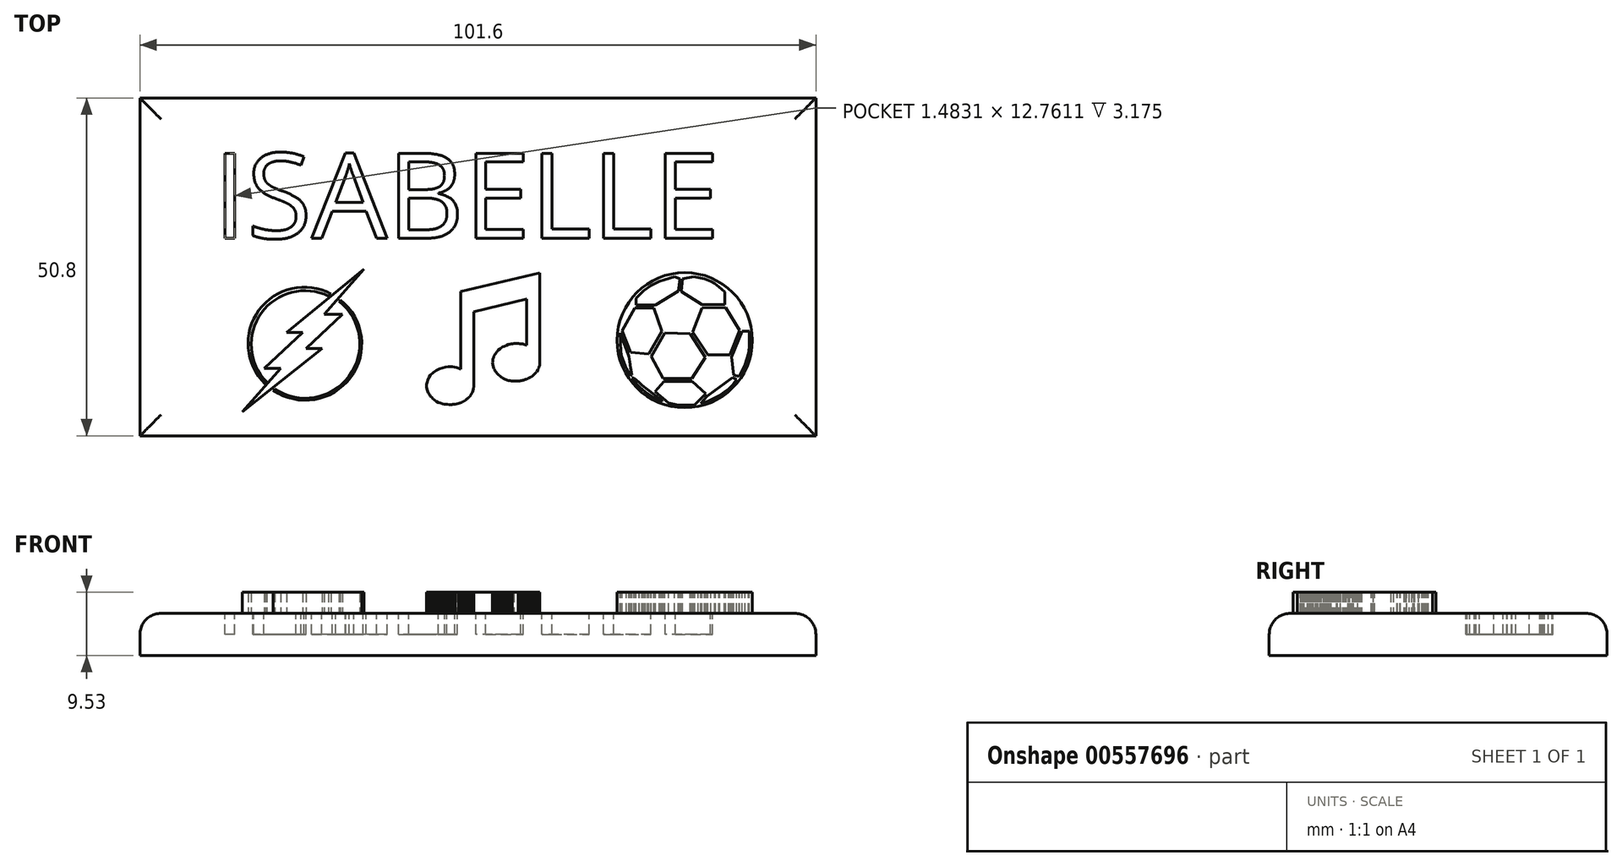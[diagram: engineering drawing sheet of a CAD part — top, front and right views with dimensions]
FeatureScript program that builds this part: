
annotation { "Feature Type Name" : "Feature", "Feature Type Description" : "" }
export const myFeature = defineFeature(function(context is Context, id is Id, definition is map)
    precondition{}
    {
        {
            var Q0;
            Q0=qCreatedBy(makeId("Top.planeOp"),FACE);
            var sketch = newSketch(context, id + "F0", { "sketchPlane" : qUnion([Q0])});
            skLineSegment(sketch, "E0.bottom", {"start": v(-50.9, 29.8) * mm, "end": v(50.7, 29.8) * mm});
            skLineSegment(sketch, "E0.top", {"start": v(-50.9, -21) * mm, "end": v(50.7, -21) * mm});
            skLineSegment(sketch, "E0.left", {"start": v(-50.9, 29.8) * mm, "end": v(-50.9, -21) * mm});
            skLineSegment(sketch, "E0.right", {"start": v(50.7, 29.8) * mm, "end": v(50.7, -21) * mm});
            skSolve(sketch);
        }
        {
            var Q0;
            Q0=makeQuery(id+"F0.imprint","IMPRINT",FACE,{"disambiguationData":[TD([[makeQuery(id+"F0.imprint","IMPRINT",EDGE,{"derivedFrom":sQuery(id+"F0.wireOp",EDGE,"E0.bottom")}),-1.0]])]});
            extrude(context, id + "F1", {"entities" : qUnion([Q0]), "depth" : 6.35 * mm, "offsetDistance" : 25.4 * mm});
        }
        {
            var Q0;
            Q0=makeQuery(id+"F1.opExtrude","CAP_FACE",FACE,{"disambiguationData":[OSD([sQuery(id+"F0.wireOp",EDGE,"E0.bottom"),sQuery(id+"F0.wireOp",EDGE,"E0.top"),sQuery(id+"F0.wireOp",EDGE,"E0.left"),sQuery(id+"F0.wireOp",EDGE,"E0.right")])],"isStart":false});
            var sketch = newSketch(context, id + "F2", { "sketchPlane" : qUnion([Q0])});
            skText(sketch, "E1", { "text": "ISABELLE", "fontName": "OpenSans-Regular.ttf"});
            const initialGuessF2  = {"E1": [-0.03987, 0.00873, 1, 0, 0.01287]};
            skSetInitialGuess(sketch, initialGuessF2);
            skSolve(sketch);
        }
        {
            var Q0;
            Q0 = qSketchRegion(id + "F2", true);
            extrude(context, id + "F3", {"entities" : qUnion([Q0]), "operationType" : NewBodyOperationType.REMOVE, "oppositeDirection" : true, "depth" : 3.17 * mm, "offsetDistance" : 25.4 * mm});
        }
        {
            var Q0;
            {var subQ0=sQuery(id+"F0.wireOp",EDGE,"E0.left");var subQ1=sQuery(id+"F0.wireOp",EDGE,"E0.bottom");var subQ2=sQuery(id+"F0.wireOp",EDGE,"E0.right");var subQ3=sQuery(id+"F0.wireOp",EDGE,"E0.top");Q0=makeQuery(id+"F3.boolean.opBoolean","SPLIT",FACE,{"disambiguationData":[TD([makeQuery(id+"F1.opExtrude","SWEPT_FACE",FACE,{"disambiguationData":[OSD([subQ1])]})])],"derivedFrom":makeQuery(id+"F1.opExtrude","CAP_FACE",FACE,{"disambiguationData":[OSD([subQ1,subQ3,subQ0,subQ2])],"isStart":false})});}
            var sketch = newSketch(context, id + "F4", { "sketchPlane" : qUnion([Q0])});
            skLineSegment(sketch, "E2", {"start": v(-35.49, -17.39) * mm, "end": v(-29.74, -10.84) * mm});
            skLineSegment(sketch, "E3", {"start": v(-29.74, -10.84) * mm, "end": v(-32.22, -10.84) * mm});
            skLineSegment(sketch, "E4", {"start": v(-32.22, -10.84) * mm, "end": v(-26.46, -5.43) * mm});
            skLineSegment(sketch, "E5", {"start": v(-26.46, -5.43) * mm, "end": v(-28.83, -5.43) * mm});
            skLineSegment(sketch, "E6", {"start": v(-28.83, -5.43) * mm, "end": v(-17.22, 4.04) * mm});
            skLineSegment(sketch, "E7", {"start": v(-17.22, 4.04) * mm, "end": v(-23.2, -2.75) * mm});
            skLineSegment(sketch, "E8", {"start": v(-23.2, -2.75) * mm, "end": v(-20.49, -2.75) * mm});
            skLineSegment(sketch, "E9", {"start": v(-20.49, -2.75) * mm, "end": v(-25.93, -7.87) * mm});
            skLineSegment(sketch, "E10", {"start": v(-25.93, -7.87) * mm, "end": v(-23.53, -7.87) * mm});
            skLineSegment(sketch, "E11", {"start": v(-23.53, -7.87) * mm, "end": v(-35.49, -17.39) * mm});
            skArc(sketch, "E12", {"start": v(-22.55, 0) * mm, "mid": v(-32.65, -2.52) * mm, "end": v(-31.86, -12.9) * mm});
            skLineSegment(sketch, "E13", {"start": v(-31.86, -12.9) * mm, "end": v(-32.08, -13.18) * mm});
            skArc(sketch, "E14", {"start": v(-22.17, 0.36) * mm, "mid": v(-33.02, -2.1) * mm, "end": v(-32.08, -13.18) * mm});
            skLineSegment(sketch, "E15", {"start": v(-22.55, 0) * mm, "end": v(-22.17, 0.36) * mm});
            skLineSegment(sketch, "E16", {"start": v(-20.95, -0.76) * mm, "end": v(-20.76, -0.55) * mm});
            skArc(sketch, "E17", {"start": v(-30.61, -13.93) * mm, "mid": v(-19.45, -12) * mm, "end": v(-20.95, -0.76) * mm});
            skLineSegment(sketch, "E18", {"start": v(-30.61, -13.93) * mm, "end": v(-30.87, -14.14) * mm});
            skArc(sketch, "E19", {"start": v(-30.87, -14.14) * mm, "mid": v(-19.25, -12.23) * mm, "end": v(-20.76, -0.55) * mm});
            skSolve(sketch);
        }
        {
            var Q0;
            Q0 = qSketchRegion(id + "F4", true);
            extrude(context, id + "F5", {"entities" : qUnion([Q0]), "operationType" : NewBodyOperationType.ADD, "depth" : 3.17 * mm, "offsetDistance" : 25.4 * mm});
        }
        {
            var Q0;
            {var subQ0=sQuery(id+"F0.wireOp",EDGE,"E0.left");var subQ1=sQuery(id+"F0.wireOp",EDGE,"E0.bottom");var subQ2=sQuery(id+"F0.wireOp",EDGE,"E0.right");var subQ3=sQuery(id+"F0.wireOp",EDGE,"E0.top");Q0=makeQuery(id+"F3.boolean.opBoolean","SPLIT",FACE,{"disambiguationData":[TD([makeQuery(id+"F1.opExtrude","SWEPT_FACE",FACE,{"disambiguationData":[OSD([subQ1])]})])],"derivedFrom":makeQuery(id+"F1.opExtrude","CAP_FACE",FACE,{"disambiguationData":[OSD([subQ1,subQ3,subQ0,subQ2])],"isStart":false})});}
            var sketch = newSketch(context, id + "F6", { "sketchPlane" : qUnion([Q0])});
            skCircle(sketch, "E20", {"center": v(30.98, -6.61) * mm, "radius": 10.16 * mm});
            skSolve(sketch);
        }
        {
            var Q0;
            Q0 = qSketchRegion(id + "F6", true);
            extrude(context, id + "F7", {"entities" : qUnion([Q0]), "operationType" : NewBodyOperationType.ADD, "depth" : 3.17 * mm, "offsetDistance" : 25.4 * mm});
        }
        {
            var Q0;
            Q0=makeQuery(id+"F7.opExtrude","CAP_FACE",FACE,{"disambiguationData":[OSD([sQuery(id+"F6.wireOp",EDGE,"E20")])],"isStart":false});
            var sketch = newSketch(context, id + "F8", { "sketchPlane" : qUnion([Q0])});
            skLineSegment(sketch, "E21", {"start": v(30.27, 2.59) * mm, "end": v(29.98, 0.79) * mm});
            skLineSegment(sketch, "E22", {"start": v(29.98, 0.79) * mm, "end": v(26.57, -1.35) * mm});
            skLineSegment(sketch, "E23", {"start": v(26.57, -1.35) * mm, "end": v(23.69, -1.35) * mm});
            skLineSegment(sketch, "E24", {"start": v(23.69, -1.35) * mm, "end": v(23.69, -0.3) * mm});
            skLineSegment(sketch, "E25", {"start": v(23.69, -0.3) * mm, "end": v(24.8, 0.84) * mm});
            skLineSegment(sketch, "E26", {"start": v(24.8, 0.84) * mm, "end": v(25.86, 1.57) * mm});
            skLineSegment(sketch, "E27", {"start": v(25.86, 1.57) * mm, "end": v(27.16, 2.22) * mm});
            skLineSegment(sketch, "E28", {"start": v(27.16, 2.22) * mm, "end": v(28, 2.5) * mm});
            skLineSegment(sketch, "E29", {"start": v(28, 2.5) * mm, "end": v(29.44, 2.92) * mm});
            skLineSegment(sketch, "E30", {"start": v(29.44, 2.92) * mm, "end": v(30.27, 2.59) * mm});
            skLineSegment(sketch, "E31", {"start": v(30.45, 0.68) * mm, "end": v(30.65, 2.59) * mm});
            skLineSegment(sketch, "E32", {"start": v(30.65, 2.59) * mm, "end": v(32.3, 2.92) * mm});
            skLineSegment(sketch, "E33", {"start": v(32.3, 2.92) * mm, "end": v(32.97, 2.8) * mm});
            skLineSegment(sketch, "E34", {"start": v(32.97, 2.8) * mm, "end": v(33.94, 2.59) * mm});
            skLineSegment(sketch, "E35", {"start": v(33.94, 2.59) * mm, "end": v(34.92, 2.2) * mm});
            skLineSegment(sketch, "E36", {"start": v(34.92, 2.2) * mm, "end": v(35.47, 1.94) * mm});
            skLineSegment(sketch, "E37", {"start": v(35.47, 1.94) * mm, "end": v(36.08, 1.4) * mm});
            skLineSegment(sketch, "E38", {"start": v(36.08, 1.4) * mm, "end": v(37.01, 0.63) * mm});
            skLineSegment(sketch, "E39", {"start": v(37.01, 0.63) * mm, "end": v(36.97, -1.28) * mm});
            skLineSegment(sketch, "E40", {"start": v(33.54, -1.28) * mm, "end": v(30.45, 0.68) * mm});
            skLineSegment(sketch, "E41", {"start": v(33.54, -1.28) * mm, "end": v(36.97, -1.28) * mm});
            skLineSegment(sketch, "E42", {"start": v(33.54, -1.76) * mm, "end": v(37.1, -1.73) * mm});
            skLineSegment(sketch, "E43", {"start": v(37.1, -1.73) * mm, "end": v(39.2, -5.15) * mm});
            skLineSegment(sketch, "E44", {"start": v(39.2, -5.15) * mm, "end": v(37.77, -8.8) * mm});
            skLineSegment(sketch, "E45", {"start": v(37.77, -8.8) * mm, "end": v(34.43, -8.8) * mm});
            skLineSegment(sketch, "E46", {"start": v(34.43, -8.8) * mm, "end": v(32.15, -5.37) * mm});
            skLineSegment(sketch, "E47", {"start": v(32.15, -5.37) * mm, "end": v(33.54, -1.76) * mm});
            skLineSegment(sketch, "E48", {"start": v(31.82, -5.63) * mm, "end": v(27.97, -5.53) * mm});
            skLineSegment(sketch, "E49", {"start": v(27.97, -5.53) * mm, "end": v(25.93, -9.06) * mm});
            skLineSegment(sketch, "E50", {"start": v(25.93, -9.06) * mm, "end": v(27.73, -12.36) * mm});
            skLineSegment(sketch, "E51", {"start": v(27.73, -12.36) * mm, "end": v(32.02, -12.36) * mm});
            skLineSegment(sketch, "E52", {"start": v(32.02, -12.36) * mm, "end": v(34.05, -9.17) * mm});
            skLineSegment(sketch, "E53", {"start": v(34.05, -9.17) * mm, "end": v(31.82, -5.63) * mm});
            skLineSegment(sketch, "E54", {"start": v(26.33, -1.76) * mm, "end": v(23.45, -1.76) * mm});
            skLineSegment(sketch, "E55", {"start": v(23.45, -1.76) * mm, "end": v(21.59, -5.2) * mm});
            skLineSegment(sketch, "E56", {"start": v(21.59, -5.2) * mm, "end": v(22.83, -8.47) * mm});
            skLineSegment(sketch, "E57", {"start": v(22.83, -8.47) * mm, "end": v(25.6, -8.67) * mm});
            skLineSegment(sketch, "E58", {"start": v(25.6, -8.67) * mm, "end": v(27.57, -5.25) * mm});
            skLineSegment(sketch, "E59", {"start": v(27.57, -5.25) * mm, "end": v(26.33, -1.76) * mm});
            skLineSegment(sketch, "E60", {"start": v(21.26, -5.53) * mm, "end": v(21.35, -8.3) * mm});
            skLineSegment(sketch, "E61", {"start": v(21.35, -8.3) * mm, "end": v(21.5, -9.06) * mm});
            skLineSegment(sketch, "E62", {"start": v(21.5, -9.06) * mm, "end": v(21.93, -10.2) * mm});
            skLineSegment(sketch, "E63", {"start": v(21.93, -10.2) * mm, "end": v(22.2, -10.89) * mm});
            skLineSegment(sketch, "E64", {"start": v(22.2, -10.89) * mm, "end": v(22.62, -11.7) * mm});
            skLineSegment(sketch, "E65", {"start": v(22.62, -11.7) * mm, "end": v(22.8, -11.98) * mm});
            skLineSegment(sketch, "E66", {"start": v(22.8, -11.98) * mm, "end": v(23.06, -11.89) * mm});
            skLineSegment(sketch, "E67", {"start": v(23.06, -11.89) * mm, "end": v(22.85, -10.76) * mm});
            skLineSegment(sketch, "E68", {"start": v(22.85, -10.76) * mm, "end": v(22.7, -9.8) * mm});
            skLineSegment(sketch, "E69", {"start": v(22.7, -9.8) * mm, "end": v(22.6, -9.06) * mm});
            skLineSegment(sketch, "E70", {"start": v(22.6, -9.06) * mm, "end": v(22.2, -8.01) * mm});
            skLineSegment(sketch, "E71", {"start": v(22.2, -8.01) * mm, "end": v(21.26, -5.53) * mm});
            skLineSegment(sketch, "E72", {"start": v(23.06, -12.31) * mm, "end": v(23.33, -12.31) * mm});
            skLineSegment(sketch, "E73", {"start": v(23.33, -12.31) * mm, "end": v(24.08, -12.94) * mm});
            skLineSegment(sketch, "E74", {"start": v(24.08, -12.94) * mm, "end": v(24.55, -13.36) * mm});
            skLineSegment(sketch, "E75", {"start": v(24.55, -13.36) * mm, "end": v(25.38, -14.05) * mm});
            skLineSegment(sketch, "E76", {"start": v(25.38, -14.05) * mm, "end": v(26.44, -14.86) * mm});
            skLineSegment(sketch, "E77", {"start": v(26.44, -14.86) * mm, "end": v(27.62, -15.77) * mm});
            skLineSegment(sketch, "E78", {"start": v(27.62, -15.77) * mm, "end": v(27.6, -15.82) * mm});
            skLineSegment(sketch, "E79", {"start": v(27.6, -15.82) * mm, "end": v(27.29, -15.72) * mm});
            skLineSegment(sketch, "E80", {"start": v(27.29, -15.72) * mm, "end": v(26.4, -15.27) * mm});
            skLineSegment(sketch, "E81", {"start": v(26.4, -15.27) * mm, "end": v(25.07, -14.43) * mm});
            skLineSegment(sketch, "E82", {"start": v(25.07, -14.43) * mm, "end": v(24.2, -13.64) * mm});
            skLineSegment(sketch, "E83", {"start": v(24.2, -13.64) * mm, "end": v(23.34, -12.74) * mm});
            skLineSegment(sketch, "E84", {"start": v(23.34, -12.74) * mm, "end": v(23.06, -12.31) * mm});
            skLineSegment(sketch, "E85", {"start": v(26.53, -14.37) * mm, "end": v(27.88, -12.85) * mm});
            skLineSegment(sketch, "E86", {"start": v(27.88, -12.85) * mm, "end": v(32.09, -12.85) * mm});
            skLineSegment(sketch, "E87", {"start": v(32.09, -12.85) * mm, "end": v(34.13, -14.66) * mm});
            skLineSegment(sketch, "E88", {"start": v(34.13, -14.66) * mm, "end": v(32.51, -16.3) * mm});
            skLineSegment(sketch, "E89", {"start": v(32.51, -16.3) * mm, "end": v(30.03, -16.35) * mm});
            skLineSegment(sketch, "E90", {"start": v(30.03, -16.35) * mm, "end": v(28.58, -16.08) * mm});
            skLineSegment(sketch, "E91", {"start": v(28.58, -16.08) * mm, "end": v(26.53, -14.37) * mm});
            skLineSegment(sketch, "E92", {"start": v(39.63, -5.29) * mm, "end": v(40.67, -5.29) * mm});
            skLineSegment(sketch, "E93", {"start": v(40.67, -5.29) * mm, "end": v(40.67, -7.67) * mm});
            skLineSegment(sketch, "E94", {"start": v(40.67, -7.67) * mm, "end": v(40.52, -8.6) * mm});
            skLineSegment(sketch, "E95", {"start": v(40.52, -8.6) * mm, "end": v(40.05, -10.3) * mm});
            skLineSegment(sketch, "E96", {"start": v(40.05, -10.3) * mm, "end": v(39.17, -12.03) * mm});
            skLineSegment(sketch, "E97", {"start": v(39.17, -12.03) * mm, "end": v(38.31, -11.84) * mm});
            skLineSegment(sketch, "E98", {"start": v(38.31, -11.84) * mm, "end": v(38, -9.14) * mm});
            skLineSegment(sketch, "E99", {"start": v(38, -9.14) * mm, "end": v(39.63, -5.29) * mm});
            skLineSegment(sketch, "E100", {"start": v(38.11, -12.26) * mm, "end": v(38.8, -12.5) * mm});
            skLineSegment(sketch, "E101", {"start": v(38.8, -12.5) * mm, "end": v(38.19, -13.33) * mm});
            skLineSegment(sketch, "E102", {"start": v(38.19, -13.33) * mm, "end": v(37.55, -13.93) * mm});
            skLineSegment(sketch, "E103", {"start": v(37.55, -13.93) * mm, "end": v(36.93, -14.42) * mm});
            skLineSegment(sketch, "E104", {"start": v(36.93, -14.42) * mm, "end": v(36.23, -14.9) * mm});
            skLineSegment(sketch, "E105", {"start": v(36.23, -14.9) * mm, "end": v(35.6, -15.26) * mm});
            skLineSegment(sketch, "E106", {"start": v(35.6, -15.26) * mm, "end": v(34.44, -15.78) * mm});
            skLineSegment(sketch, "E107", {"start": v(34.44, -15.78) * mm, "end": v(33.35, -16.1) * mm});
            skLineSegment(sketch, "E108", {"start": v(33.35, -16.1) * mm, "end": v(34.35, -15.02) * mm});
            skLineSegment(sketch, "E109", {"start": v(34.35, -15.02) * mm, "end": v(35.55, -14.16) * mm});
            skLineSegment(sketch, "E110", {"start": v(35.55, -14.16) * mm, "end": v(36.93, -13.16) * mm});
            skLineSegment(sketch, "E111", {"start": v(36.93, -13.16) * mm, "end": v(38.11, -12.26) * mm});
            skPoint(sketch, "E112.endSnap0", {"position": v(34.95, -14.59) * mm});
            skSolve(sketch);
        }
        {
            var Q0;
            Q0 = qSketchRegion(id + "F8", true);
            extrude(context, id + "F9", {"entities" : qUnion([Q0]), "operationType" : NewBodyOperationType.REMOVE, "oppositeDirection" : true, "depth" : 3.17 * mm, "offsetDistance" : 25.4 * mm});
        }
        {
            var Q0;
            {var subQ0=sQuery(id+"F0.wireOp",EDGE,"E0.left");var subQ1=sQuery(id+"F0.wireOp",EDGE,"E0.bottom");var subQ2=sQuery(id+"F0.wireOp",EDGE,"E0.right");var subQ3=sQuery(id+"F0.wireOp",EDGE,"E0.top");Q0=makeQuery(id+"F3.boolean.opBoolean","SPLIT",FACE,{"disambiguationData":[TD([makeQuery(id+"F1.opExtrude","SWEPT_FACE",FACE,{"disambiguationData":[OSD([subQ1])]})])],"derivedFrom":makeQuery(id+"F1.opExtrude","CAP_FACE",FACE,{"disambiguationData":[OSD([subQ1,subQ3,subQ0,subQ2])],"isStart":false})});}
            var sketch = newSketch(context, id + "F10", { "sketchPlane" : qUnion([Q0])});
            skLineSegment(sketch, "E113", {"start": v(-2.7, -10.98) * mm, "end": v(-2.96, -10.85) * mm});
            skLineSegment(sketch, "E114", {"start": v(-2.96, -10.85) * mm, "end": v(-3.32, -10.74) * mm});
            skLineSegment(sketch, "E115", {"start": v(-3.32, -10.74) * mm, "end": v(-3.65, -10.68) * mm});
            skLineSegment(sketch, "E116", {"start": v(-3.65, -10.68) * mm, "end": v(-3.97, -10.62) * mm});
            skLineSegment(sketch, "E117", {"start": v(-3.97, -10.62) * mm, "end": v(-4.3, -10.62) * mm});
            skLineSegment(sketch, "E118", {"start": v(-4.3, -10.62) * mm, "end": v(-4.6, -10.62) * mm});
            skLineSegment(sketch, "E119", {"start": v(-4.6, -10.62) * mm, "end": v(-4.97, -10.68) * mm});
            skLineSegment(sketch, "E120", {"start": v(-4.97, -10.68) * mm, "end": v(-5.42, -10.77) * mm});
            skLineSegment(sketch, "E121", {"start": v(-5.42, -10.77) * mm, "end": v(-5.89, -10.93) * mm});
            skLineSegment(sketch, "E122", {"start": v(-5.89, -10.93) * mm, "end": v(-6.37, -11.19) * mm});
            skLineSegment(sketch, "E123", {"start": v(-6.37, -11.19) * mm, "end": v(-6.85, -11.5) * mm});
            skLineSegment(sketch, "E124", {"start": v(-6.85, -11.5) * mm, "end": v(-7.23, -11.9) * mm});
            skLineSegment(sketch, "E125", {"start": v(-7.23, -11.9) * mm, "end": v(-7.44, -12.18) * mm});
            skLineSegment(sketch, "E126", {"start": v(-7.44, -12.18) * mm, "end": v(-7.65, -12.63) * mm});
            skLineSegment(sketch, "E127", {"start": v(-7.65, -12.63) * mm, "end": v(-7.74, -12.9) * mm});
            skLineSegment(sketch, "E128", {"start": v(-7.74, -12.9) * mm, "end": v(-7.83, -13.29) * mm});
            skLineSegment(sketch, "E129", {"start": v(-7.83, -13.29) * mm, "end": v(-7.83, -13.73) * mm});
            skLineSegment(sketch, "E130", {"start": v(-7.83, -13.73) * mm, "end": v(-7.74, -14.13) * mm});
            skLineSegment(sketch, "E131", {"start": v(-7.74, -14.13) * mm, "end": v(-7.57, -14.53) * mm});
            skLineSegment(sketch, "E132", {"start": v(-7.57, -14.53) * mm, "end": v(-7.43, -14.76) * mm});
            skLineSegment(sketch, "E133", {"start": v(-7.43, -14.76) * mm, "end": v(-7.36, -14.88) * mm});
            skLineSegment(sketch, "E134", {"start": v(-7.36, -14.88) * mm, "end": v(-7.24, -15.03) * mm});
            skLineSegment(sketch, "E135", {"start": v(-7.24, -15.03) * mm, "end": v(-7.1, -15.19) * mm});
            skLineSegment(sketch, "E136", {"start": v(-7.1, -15.19) * mm, "end": v(-7.04, -15.26) * mm});
            skLineSegment(sketch, "E137", {"start": v(-7.04, -15.26) * mm, "end": v(-6.89, -15.4) * mm});
            skLineSegment(sketch, "E138", {"start": v(-6.89, -15.4) * mm, "end": v(-6.72, -15.53) * mm});
            skLineSegment(sketch, "E139", {"start": v(-6.72, -15.53) * mm, "end": v(-6.53, -15.67) * mm});
            skLineSegment(sketch, "E140", {"start": v(-6.53, -15.67) * mm, "end": v(-6.36, -15.8) * mm});
            skLineSegment(sketch, "E141", {"start": v(-6.36, -15.8) * mm, "end": v(-6.04, -15.96) * mm});
            skLineSegment(sketch, "E142", {"start": v(-6.04, -15.96) * mm, "end": v(-5.74, -16.09) * mm});
            skLineSegment(sketch, "E143", {"start": v(-5.74, -16.09) * mm, "end": v(-5.42, -16.2) * mm});
            skLineSegment(sketch, "E144", {"start": v(-5.42, -16.2) * mm, "end": v(-5.14, -16.25) * mm});
            skLineSegment(sketch, "E145", {"start": v(-5.14, -16.25) * mm, "end": v(-4.88, -16.28) * mm});
            skLineSegment(sketch, "E146", {"start": v(-4.88, -16.28) * mm, "end": v(-4.69, -16.28) * mm});
            skLineSegment(sketch, "E147", {"start": v(-4.69, -16.28) * mm, "end": v(-4.55, -16.3) * mm});
            skLineSegment(sketch, "E148", {"start": v(-4.55, -16.3) * mm, "end": v(-4.39, -16.3) * mm});
            skLineSegment(sketch, "E149", {"start": v(-4.39, -16.3) * mm, "end": v(-4.22, -16.3) * mm});
            skLineSegment(sketch, "E150", {"start": v(-4.22, -16.3) * mm, "end": v(-4, -16.3) * mm});
            skLineSegment(sketch, "E151", {"start": v(-4, -16.3) * mm, "end": v(-3.87, -16.28) * mm});
            skLineSegment(sketch, "E152", {"start": v(-3.87, -16.28) * mm, "end": v(-3.68, -16.26) * mm});
            skLineSegment(sketch, "E153", {"start": v(-3.68, -16.26) * mm, "end": v(-3.5, -16.22) * mm});
            skLineSegment(sketch, "E154", {"start": v(-3.5, -16.22) * mm, "end": v(-3.35, -16.19) * mm});
            skLineSegment(sketch, "E155", {"start": v(-3.35, -16.19) * mm, "end": v(-3.19, -16.15) * mm});
            skLineSegment(sketch, "E156", {"start": v(-3.19, -16.15) * mm, "end": v(-3.02, -16.11) * mm});
            skLineSegment(sketch, "E157", {"start": v(-3.02, -16.11) * mm, "end": v(-2.87, -16.07) * mm});
            skLineSegment(sketch, "E158", {"start": v(-2.87, -16.07) * mm, "end": v(-2.76, -16.03) * mm});
            skLineSegment(sketch, "E159", {"start": v(-2.76, -16.03) * mm, "end": v(-2.65, -16) * mm});
            skLineSegment(sketch, "E160", {"start": v(-2.65, -16) * mm, "end": v(-2.56, -15.95) * mm});
            skLineSegment(sketch, "E161", {"start": v(-2.56, -15.95) * mm, "end": v(-2.46, -15.9) * mm});
            skLineSegment(sketch, "E162", {"start": v(-2.46, -15.9) * mm, "end": v(-2.37, -15.86) * mm});
            skLineSegment(sketch, "E163", {"start": v(-2.37, -15.86) * mm, "end": v(-2.27, -15.81) * mm});
            skLineSegment(sketch, "E164", {"start": v(-2.27, -15.81) * mm, "end": v(-2.2, -15.77) * mm});
            skLineSegment(sketch, "E165", {"start": v(-2.2, -15.77) * mm, "end": v(-2.14, -15.74) * mm});
            skLineSegment(sketch, "E166", {"start": v(-2.14, -15.74) * mm, "end": v(-2.08, -15.7) * mm});
            skLineSegment(sketch, "E167", {"start": v(-2.08, -15.7) * mm, "end": v(-2.01, -15.65) * mm});
            skLineSegment(sketch, "E168", {"start": v(-2.01, -15.65) * mm, "end": v(-1.96, -15.62) * mm});
            skLineSegment(sketch, "E169", {"start": v(-1.96, -15.62) * mm, "end": v(-1.92, -15.59) * mm});
            skLineSegment(sketch, "E170", {"start": v(-1.92, -15.59) * mm, "end": v(-1.9, -15.56) * mm});
            skLineSegment(sketch, "E171", {"start": v(-1.9, -15.56) * mm, "end": v(-1.84, -15.53) * mm});
            skLineSegment(sketch, "E172", {"start": v(-1.84, -15.53) * mm, "end": v(-1.79, -15.5) * mm});
            skLineSegment(sketch, "E173", {"start": v(-1.79, -15.5) * mm, "end": v(-1.75, -15.45) * mm});
            skLineSegment(sketch, "E174", {"start": v(-1.75, -15.45) * mm, "end": v(-1.7, -15.42) * mm});
            skLineSegment(sketch, "E175", {"start": v(-1.7, -15.42) * mm, "end": v(-1.67, -15.38) * mm});
            skLineSegment(sketch, "E176", {"start": v(-1.67, -15.38) * mm, "end": v(-1.63, -15.34) * mm});
            skLineSegment(sketch, "E177", {"start": v(-1.63, -15.34) * mm, "end": v(-1.59, -15.3) * mm});
            skLineSegment(sketch, "E178", {"start": v(-1.59, -15.3) * mm, "end": v(-1.55, -15.28) * mm});
            skLineSegment(sketch, "E179", {"start": v(-1.55, -15.28) * mm, "end": v(-1.52, -15.23) * mm});
            skLineSegment(sketch, "E180", {"start": v(-1.52, -15.23) * mm, "end": v(-1.48, -15.2) * mm});
            skLineSegment(sketch, "E181", {"start": v(-1.48, -15.2) * mm, "end": v(-1.43, -15.16) * mm});
            skLineSegment(sketch, "E182", {"start": v(-1.43, -15.16) * mm, "end": v(-1.41, -15.13) * mm});
            skLineSegment(sketch, "E183", {"start": v(-1.41, -15.13) * mm, "end": v(-1.38, -15.09) * mm});
            skLineSegment(sketch, "E184", {"start": v(-1.38, -15.09) * mm, "end": v(-1.34, -15.05) * mm});
            skLineSegment(sketch, "E185", {"start": v(-1.34, -15.05) * mm, "end": v(-1.3, -15.01) * mm});
            skLineSegment(sketch, "E186", {"start": v(-1.3, -15.01) * mm, "end": v(-1.26, -14.96) * mm});
            skLineSegment(sketch, "E187", {"start": v(-1.26, -14.96) * mm, "end": v(-1.22, -14.9) * mm});
            skLineSegment(sketch, "E188", {"start": v(-1.22, -14.9) * mm, "end": v(-1.17, -14.85) * mm});
            skLineSegment(sketch, "E189", {"start": v(-1.17, -14.85) * mm, "end": v(-1.14, -14.8) * mm});
            skLineSegment(sketch, "E190", {"start": v(-1.14, -14.8) * mm, "end": v(-1.1, -14.76) * mm});
            skLineSegment(sketch, "E191", {"start": v(-1.1, -14.76) * mm, "end": v(-1.07, -14.7) * mm});
            skLineSegment(sketch, "E192", {"start": v(-1.07, -14.7) * mm, "end": v(-1.05, -14.66) * mm});
            skLineSegment(sketch, "E193", {"start": v(-1.05, -14.66) * mm, "end": v(-1.02, -14.62) * mm});
            skLineSegment(sketch, "E194", {"start": v(-1.02, -14.62) * mm, "end": v(-1, -14.57) * mm});
            skLineSegment(sketch, "E195", {"start": v(-1, -14.57) * mm, "end": v(-0.96, -14.5) * mm});
            skLineSegment(sketch, "E196", {"start": v(-0.96, -14.5) * mm, "end": v(-0.95, -14.46) * mm});
            skLineSegment(sketch, "E197", {"start": v(-0.95, -14.46) * mm, "end": v(-0.92, -14.41) * mm});
            skLineSegment(sketch, "E198", {"start": v(-0.92, -14.41) * mm, "end": v(-0.9, -14.38) * mm});
            skLineSegment(sketch, "E199", {"start": v(-0.9, -14.38) * mm, "end": v(-0.9, -14.33) * mm});
            skLineSegment(sketch, "E200", {"start": v(-0.9, -14.33) * mm, "end": v(-0.86, -14.22) * mm});
            skLineSegment(sketch, "E201", {"start": v(-0.86, -14.22) * mm, "end": v(-0.8, -14.09) * mm});
            skLineSegment(sketch, "E202", {"start": v(-0.8, -14.09) * mm, "end": v(-0.76, -13.94) * mm});
            skLineSegment(sketch, "E203", {"start": v(-0.76, -13.94) * mm, "end": v(-0.75, -13.81) * mm});
            skLineSegment(sketch, "E204", {"start": v(-0.75, -13.81) * mm, "end": v(-0.73, -13.69) * mm});
            skLineSegment(sketch, "E205", {"start": v(-0.73, -13.69) * mm, "end": v(-0.72, -13.54) * mm});
            skLineSegment(sketch, "E206", {"start": v(-0.72, -13.54) * mm, "end": v(-0.72, -13.4) * mm});
            skLineSegment(sketch, "E207", {"start": v(-0.72, -13.4) * mm, "end": v(-0.72, -13.18) * mm});
            skLineSegment(sketch, "E208", {"start": v(-0.72, -13.18) * mm, "end": v(-0.72, -12.82) * mm});
            skLineSegment(sketch, "E209", {"start": v(-0.72, -12.82) * mm, "end": v(-0.72, -2.34) * mm});
            skLineSegment(sketch, "E210", {"start": v(-0.72, -2.34) * mm, "end": v(7.16, -0.44) * mm});
            skLineSegment(sketch, "E211", {"start": v(7.16, -0.44) * mm, "end": v(7.22, -0.44) * mm});
            skLineSegment(sketch, "E212", {"start": v(7.22, -0.44) * mm, "end": v(7.22, -7.38) * mm});
            skLineSegment(sketch, "E213", {"start": v(7.22, -7.38) * mm, "end": v(7.13, -7.35) * mm});
            skLineSegment(sketch, "E214", {"start": v(7.13, -7.35) * mm, "end": v(7.03, -7.32) * mm});
            skLineSegment(sketch, "E215", {"start": v(7.03, -7.32) * mm, "end": v(6.95, -7.29) * mm});
            skLineSegment(sketch, "E216", {"start": v(6.95, -7.29) * mm, "end": v(6.86, -7.26) * mm});
            skLineSegment(sketch, "E217", {"start": v(6.86, -7.26) * mm, "end": v(6.76, -7.22) * mm});
            skLineSegment(sketch, "E218", {"start": v(6.76, -7.22) * mm, "end": v(6.64, -7.2) * mm});
            skLineSegment(sketch, "E219", {"start": v(6.64, -7.2) * mm, "end": v(6.52, -7.17) * mm});
            skLineSegment(sketch, "E220", {"start": v(6.52, -7.17) * mm, "end": v(6.4, -7.16) * mm});
            skLineSegment(sketch, "E221", {"start": v(6.4, -7.16) * mm, "end": v(6.27, -7.15) * mm});
            skLineSegment(sketch, "E222", {"start": v(6.27, -7.15) * mm, "end": v(6.16, -7.14) * mm});
            skLineSegment(sketch, "E223", {"start": v(6.16, -7.14) * mm, "end": v(6.04, -7.11) * mm});
            skLineSegment(sketch, "E224", {"start": v(6.04, -7.11) * mm, "end": v(5.9, -7.11) * mm});
            skLineSegment(sketch, "E225", {"start": v(5.9, -7.11) * mm, "end": v(5.77, -7.11) * mm});
            skLineSegment(sketch, "E226", {"start": v(5.77, -7.11) * mm, "end": v(5.48, -7.11) * mm});
            skLineSegment(sketch, "E227", {"start": v(5.48, -7.11) * mm, "end": v(5.3, -7.11) * mm});
            skLineSegment(sketch, "E228", {"start": v(5.3, -7.11) * mm, "end": v(5.23, -7.13) * mm});
            skLineSegment(sketch, "E229", {"start": v(5.23, -7.13) * mm, "end": v(5.17, -7.15) * mm});
            skLineSegment(sketch, "E230", {"start": v(5.17, -7.15) * mm, "end": v(5.12, -7.15) * mm});
            skLineSegment(sketch, "E231", {"start": v(5.12, -7.15) * mm, "end": v(5.04, -7.16) * mm});
            skLineSegment(sketch, "E232", {"start": v(5.04, -7.16) * mm, "end": v(5, -7.16) * mm});
            skLineSegment(sketch, "E233", {"start": v(5, -7.16) * mm, "end": v(4.94, -7.18) * mm});
            skLineSegment(sketch, "E234", {"start": v(4.94, -7.18) * mm, "end": v(4.89, -7.19) * mm});
            skLineSegment(sketch, "E235", {"start": v(4.89, -7.19) * mm, "end": v(4.85, -7.2) * mm});
            skLineSegment(sketch, "E236", {"start": v(4.85, -7.2) * mm, "end": v(4.8, -7.2) * mm});
            skLineSegment(sketch, "E237", {"start": v(4.8, -7.2) * mm, "end": v(4.76, -7.2) * mm});
            skLineSegment(sketch, "E238", {"start": v(4.76, -7.2) * mm, "end": v(4.72, -7.21) * mm});
            skLineSegment(sketch, "E239", {"start": v(4.72, -7.21) * mm, "end": v(4.7, -7.22) * mm});
            skLineSegment(sketch, "E240", {"start": v(4.7, -7.22) * mm, "end": v(4.66, -7.23) * mm});
            skLineSegment(sketch, "E241", {"start": v(4.66, -7.23) * mm, "end": v(4.62, -7.23) * mm});
            skLineSegment(sketch, "E242", {"start": v(4.62, -7.23) * mm, "end": v(4.58, -7.24) * mm});
            skLineSegment(sketch, "E243", {"start": v(4.58, -7.24) * mm, "end": v(4.5, -7.25) * mm});
            skLineSegment(sketch, "E244", {"start": v(4.5, -7.25) * mm, "end": v(4.41, -7.29) * mm});
            skLineSegment(sketch, "E245", {"start": v(4.41, -7.29) * mm, "end": v(4.29, -7.34) * mm});
            skLineSegment(sketch, "E246", {"start": v(4.29, -7.34) * mm, "end": v(4.16, -7.4) * mm});
            skLineSegment(sketch, "E247", {"start": v(4.16, -7.4) * mm, "end": v(4.05, -7.42) * mm});
            skLineSegment(sketch, "E248", {"start": v(4.05, -7.42) * mm, "end": v(3.96, -7.46) * mm});
            skLineSegment(sketch, "E249", {"start": v(3.96, -7.46) * mm, "end": v(3.86, -7.53) * mm});
            skLineSegment(sketch, "E250", {"start": v(3.86, -7.53) * mm, "end": v(3.77, -7.57) * mm});
            skLineSegment(sketch, "E251", {"start": v(3.77, -7.57) * mm, "end": v(3.62, -7.64) * mm});
            skLineSegment(sketch, "E252", {"start": v(3.62, -7.64) * mm, "end": v(3.49, -7.73) * mm});
            skLineSegment(sketch, "E253", {"start": v(3.49, -7.73) * mm, "end": v(3.39, -7.8) * mm});
            skLineSegment(sketch, "E254", {"start": v(3.39, -7.8) * mm, "end": v(3.3, -7.87) * mm});
            skLineSegment(sketch, "E255", {"start": v(3.3, -7.87) * mm, "end": v(3.2, -7.91) * mm});
            skLineSegment(sketch, "E256", {"start": v(3.2, -7.91) * mm, "end": v(3.12, -7.97) * mm});
            skLineSegment(sketch, "E257", {"start": v(3.12, -7.97) * mm, "end": v(3, -8.05) * mm});
            skLineSegment(sketch, "E258", {"start": v(3, -8.05) * mm, "end": v(2.9, -8.13) * mm});
            skLineSegment(sketch, "E259", {"start": v(2.9, -8.13) * mm, "end": v(2.87, -8.2) * mm});
            skLineSegment(sketch, "E260", {"start": v(2.87, -8.2) * mm, "end": v(2.78, -8.3) * mm});
            skLineSegment(sketch, "E261", {"start": v(2.78, -8.3) * mm, "end": v(2.68, -8.42) * mm});
            skLineSegment(sketch, "E262", {"start": v(2.68, -8.42) * mm, "end": v(2.62, -8.51) * mm});
            skLineSegment(sketch, "E263", {"start": v(2.62, -8.51) * mm, "end": v(2.54, -8.64) * mm});
            skLineSegment(sketch, "E264", {"start": v(2.54, -8.64) * mm, "end": v(2.47, -8.74) * mm});
            skLineSegment(sketch, "E265", {"start": v(2.47, -8.74) * mm, "end": v(2.43, -8.8) * mm});
            skLineSegment(sketch, "E266", {"start": v(2.43, -8.8) * mm, "end": v(2.39, -8.87) * mm});
            skLineSegment(sketch, "E267", {"start": v(2.39, -8.87) * mm, "end": v(2.35, -8.93) * mm});
            skLineSegment(sketch, "E268", {"start": v(2.35, -8.93) * mm, "end": v(2.33, -9) * mm});
            skLineSegment(sketch, "E269", {"start": v(2.33, -9) * mm, "end": v(2.28, -9.09) * mm});
            skLineSegment(sketch, "E270", {"start": v(2.28, -9.09) * mm, "end": v(2.25, -9.18) * mm});
            skLineSegment(sketch, "E271", {"start": v(2.25, -9.18) * mm, "end": v(2.22, -9.27) * mm});
            skLineSegment(sketch, "E272", {"start": v(2.22, -9.27) * mm, "end": v(2.2, -9.33) * mm});
            skLineSegment(sketch, "E273", {"start": v(2.2, -9.33) * mm, "end": v(2.19, -9.4) * mm});
            skLineSegment(sketch, "E274", {"start": v(2.19, -9.4) * mm, "end": v(2.17, -9.46) * mm});
            skLineSegment(sketch, "E275", {"start": v(2.17, -9.46) * mm, "end": v(2.17, -9.56) * mm});
            skLineSegment(sketch, "E276", {"start": v(2.17, -9.56) * mm, "end": v(2.15, -9.63) * mm});
            skLineSegment(sketch, "E277", {"start": v(2.15, -9.63) * mm, "end": v(2.12, -9.72) * mm});
            skLineSegment(sketch, "E278", {"start": v(2.12, -9.72) * mm, "end": v(2.12, -9.82) * mm});
            skLineSegment(sketch, "E279", {"start": v(2.12, -9.82) * mm, "end": v(2.1, -9.9) * mm});
            skLineSegment(sketch, "E280", {"start": v(2.1, -9.9) * mm, "end": v(2.08, -9.99) * mm});
            skLineSegment(sketch, "E281", {"start": v(2.08, -9.99) * mm, "end": v(2.1, -10.08) * mm});
            skLineSegment(sketch, "E282", {"start": v(2.1, -10.08) * mm, "end": v(2.1, -10.19) * mm});
            skLineSegment(sketch, "E283", {"start": v(2.1, -10.19) * mm, "end": v(2.12, -10.27) * mm});
            skLineSegment(sketch, "E284", {"start": v(2.12, -10.27) * mm, "end": v(2.14, -10.39) * mm});
            skLineSegment(sketch, "E285", {"start": v(2.14, -10.39) * mm, "end": v(2.16, -10.5) * mm});
            skLineSegment(sketch, "E286", {"start": v(2.16, -10.5) * mm, "end": v(2.18, -10.6) * mm});
            skLineSegment(sketch, "E287", {"start": v(2.18, -10.6) * mm, "end": v(2.2, -10.66) * mm});
            skLineSegment(sketch, "E288", {"start": v(2.2, -10.66) * mm, "end": v(2.25, -10.77) * mm});
            skLineSegment(sketch, "E289", {"start": v(2.25, -10.77) * mm, "end": v(2.3, -10.9) * mm});
            skLineSegment(sketch, "E290", {"start": v(2.3, -10.9) * mm, "end": v(2.36, -11) * mm});
            skLineSegment(sketch, "E291", {"start": v(2.36, -11) * mm, "end": v(2.39, -11.05) * mm});
            skLineSegment(sketch, "E292", {"start": v(2.39, -11.05) * mm, "end": v(2.43, -11.15) * mm});
            skLineSegment(sketch, "E293", {"start": v(2.43, -11.15) * mm, "end": v(2.47, -11.23) * mm});
            skLineSegment(sketch, "E294", {"start": v(2.47, -11.23) * mm, "end": v(2.5, -11.29) * mm});
            skLineSegment(sketch, "E295", {"start": v(2.5, -11.29) * mm, "end": v(2.57, -11.37) * mm});
            skLineSegment(sketch, "E296", {"start": v(2.57, -11.37) * mm, "end": v(2.62, -11.42) * mm});
            skLineSegment(sketch, "E297", {"start": v(2.62, -11.42) * mm, "end": v(2.67, -11.49) * mm});
            skLineSegment(sketch, "E298", {"start": v(2.67, -11.49) * mm, "end": v(2.71, -11.55) * mm});
            skLineSegment(sketch, "E299", {"start": v(2.71, -11.55) * mm, "end": v(2.76, -11.61) * mm});
            skLineSegment(sketch, "E300", {"start": v(2.76, -11.61) * mm, "end": v(2.8, -11.65) * mm});
            skLineSegment(sketch, "E301", {"start": v(2.8, -11.65) * mm, "end": v(2.85, -11.7) * mm});
            skLineSegment(sketch, "E302", {"start": v(2.85, -11.7) * mm, "end": v(2.9, -11.74) * mm});
            skLineSegment(sketch, "E303", {"start": v(2.9, -11.74) * mm, "end": v(2.95, -11.8) * mm});
            skLineSegment(sketch, "E304", {"start": v(2.95, -11.8) * mm, "end": v(3, -11.84) * mm});
            skLineSegment(sketch, "E305", {"start": v(3, -11.84) * mm, "end": v(3.05, -11.88) * mm});
            skLineSegment(sketch, "E306", {"start": v(3.05, -11.88) * mm, "end": v(3.1, -11.92) * mm});
            skLineSegment(sketch, "E307", {"start": v(3.1, -11.92) * mm, "end": v(3.14, -11.96) * mm});
            skLineSegment(sketch, "E308", {"start": v(3.14, -11.96) * mm, "end": v(3.2, -12) * mm});
            skLineSegment(sketch, "E309", {"start": v(3.2, -12) * mm, "end": v(3.24, -12.04) * mm});
            skLineSegment(sketch, "E310", {"start": v(3.24, -12.04) * mm, "end": v(3.3, -12.07) * mm});
            skLineSegment(sketch, "E311", {"start": v(3.3, -12.07) * mm, "end": v(3.34, -12.12) * mm});
            skLineSegment(sketch, "E312", {"start": v(3.34, -12.12) * mm, "end": v(3.39, -12.15) * mm});
            skLineSegment(sketch, "E313", {"start": v(3.39, -12.15) * mm, "end": v(3.44, -12.18) * mm});
            skLineSegment(sketch, "E314", {"start": v(3.44, -12.18) * mm, "end": v(3.5, -12.22) * mm});
            skLineSegment(sketch, "E315", {"start": v(3.5, -12.22) * mm, "end": v(3.55, -12.25) * mm});
            skLineSegment(sketch, "E316", {"start": v(3.55, -12.25) * mm, "end": v(3.6, -12.28) * mm});
            skLineSegment(sketch, "E317", {"start": v(3.6, -12.28) * mm, "end": v(3.65, -12.32) * mm});
            skLineSegment(sketch, "E318", {"start": v(3.65, -12.32) * mm, "end": v(3.69, -12.33) * mm});
            skLineSegment(sketch, "E319", {"start": v(3.69, -12.33) * mm, "end": v(3.75, -12.35) * mm});
            skLineSegment(sketch, "E320", {"start": v(3.75, -12.35) * mm, "end": v(3.83, -12.4) * mm});
            skLineSegment(sketch, "E321", {"start": v(3.83, -12.4) * mm, "end": v(3.88, -12.43) * mm});
            skLineSegment(sketch, "E322", {"start": v(3.88, -12.43) * mm, "end": v(3.96, -12.48) * mm});
            skLineSegment(sketch, "E323", {"start": v(3.96, -12.48) * mm, "end": v(4.01, -12.5) * mm});
            skLineSegment(sketch, "E324", {"start": v(4.01, -12.5) * mm, "end": v(4.06, -12.52) * mm});
            skLineSegment(sketch, "E325", {"start": v(4.06, -12.52) * mm, "end": v(4.11, -12.54) * mm});
            skLineSegment(sketch, "E326", {"start": v(4.11, -12.54) * mm, "end": v(4.17, -12.57) * mm});
            skLineSegment(sketch, "E327", {"start": v(4.17, -12.57) * mm, "end": v(4.2, -12.58) * mm});
            skLineSegment(sketch, "E328", {"start": v(4.2, -12.58) * mm, "end": v(4.26, -12.62) * mm});
            skLineSegment(sketch, "E329", {"start": v(4.26, -12.62) * mm, "end": v(4.32, -12.62) * mm});
            skLineSegment(sketch, "E330", {"start": v(4.32, -12.62) * mm, "end": v(4.36, -12.63) * mm});
            skLineSegment(sketch, "E331", {"start": v(4.36, -12.63) * mm, "end": v(4.4, -12.64) * mm});
            skLineSegment(sketch, "E332", {"start": v(4.4, -12.64) * mm, "end": v(4.48, -12.66) * mm});
            skLineSegment(sketch, "E333", {"start": v(4.48, -12.66) * mm, "end": v(4.55, -12.66) * mm});
            skLineSegment(sketch, "E334", {"start": v(4.55, -12.66) * mm, "end": v(4.66, -12.68) * mm});
            skLineSegment(sketch, "E335", {"start": v(4.66, -12.68) * mm, "end": v(4.7, -12.69) * mm});
            skLineSegment(sketch, "E336", {"start": v(4.7, -12.69) * mm, "end": v(4.77, -12.72) * mm});
            skLineSegment(sketch, "E337", {"start": v(4.77, -12.72) * mm, "end": v(4.84, -12.74) * mm});
            skLineSegment(sketch, "E338", {"start": v(4.84, -12.74) * mm, "end": v(4.9, -12.75) * mm});
            skLineSegment(sketch, "E339", {"start": v(4.9, -12.75) * mm, "end": v(5.03, -12.77) * mm});
            skLineSegment(sketch, "E340", {"start": v(5.03, -12.77) * mm, "end": v(5.12, -12.77) * mm});
            skLineSegment(sketch, "E341", {"start": v(5.12, -12.77) * mm, "end": v(5.32, -12.77) * mm});
            skPoint(sketch, "E341.endSnap0", {"position": v(5.07, -12.77) * mm});
            skLineSegment(sketch, "E342", {"start": v(5.32, -12.77) * mm, "end": v(5.56, -12.77) * mm});
            skLineSegment(sketch, "E343", {"start": v(5.56, -12.77) * mm, "end": v(5.77, -12.77) * mm});
            skLineSegment(sketch, "E344", {"start": v(5.77, -12.77) * mm, "end": v(5.98, -12.77) * mm});
            skLineSegment(sketch, "E345", {"start": v(5.98, -12.77) * mm, "end": v(6.05, -12.75) * mm});
            skLineSegment(sketch, "E346", {"start": v(6.05, -12.75) * mm, "end": v(6.17, -12.73) * mm});
            skLineSegment(sketch, "E347", {"start": v(6.17, -12.73) * mm, "end": v(6.33, -12.72) * mm});
            skLineSegment(sketch, "E348", {"start": v(6.33, -12.72) * mm, "end": v(6.4, -12.7) * mm});
            skLineSegment(sketch, "E349", {"start": v(6.4, -12.7) * mm, "end": v(6.52, -12.68) * mm});
            skLineSegment(sketch, "E350", {"start": v(6.52, -12.68) * mm, "end": v(6.62, -12.66) * mm});
            skLineSegment(sketch, "E351", {"start": v(6.62, -12.66) * mm, "end": v(6.7, -12.64) * mm});
            skLineSegment(sketch, "E352", {"start": v(6.7, -12.64) * mm, "end": v(6.78, -12.6) * mm});
            skLineSegment(sketch, "E353", {"start": v(6.78, -12.6) * mm, "end": v(6.93, -12.58) * mm});
            skLineSegment(sketch, "E354", {"start": v(6.93, -12.58) * mm, "end": v(7.03, -12.53) * mm});
            skLineSegment(sketch, "E355", {"start": v(7.03, -12.53) * mm, "end": v(7.11, -12.5) * mm});
            skLineSegment(sketch, "E356", {"start": v(7.11, -12.5) * mm, "end": v(7.2, -12.48) * mm});
            skLineSegment(sketch, "E357", {"start": v(7.2, -12.48) * mm, "end": v(7.26, -12.43) * mm});
            skLineSegment(sketch, "E358", {"start": v(7.26, -12.43) * mm, "end": v(7.33, -12.4) * mm});
            skLineSegment(sketch, "E359", {"start": v(7.33, -12.4) * mm, "end": v(7.4, -12.39) * mm});
            skLineSegment(sketch, "E360", {"start": v(7.4, -12.39) * mm, "end": v(7.5, -12.35) * mm});
            skLineSegment(sketch, "E361", {"start": v(7.5, -12.35) * mm, "end": v(7.55, -12.3) * mm});
            skLineSegment(sketch, "E362", {"start": v(7.55, -12.3) * mm, "end": v(7.63, -12.28) * mm});
            skLineSegment(sketch, "E363", {"start": v(7.63, -12.28) * mm, "end": v(7.69, -12.25) * mm});
            skLineSegment(sketch, "E364", {"start": v(7.69, -12.25) * mm, "end": v(7.78, -12.21) * mm});
            skLineSegment(sketch, "E365", {"start": v(7.78, -12.21) * mm, "end": v(7.86, -12.16) * mm});
            skLineSegment(sketch, "E366", {"start": v(7.86, -12.16) * mm, "end": v(7.92, -12.1) * mm});
            skLineSegment(sketch, "E367", {"start": v(7.92, -12.1) * mm, "end": v(7.99, -12.06) * mm});
            skLineSegment(sketch, "E368", {"start": v(7.99, -12.06) * mm, "end": v(8.05, -12.01) * mm});
            skLineSegment(sketch, "E369", {"start": v(8.05, -12.01) * mm, "end": v(8.1, -11.97) * mm});
            skLineSegment(sketch, "E370", {"start": v(8.1, -11.97) * mm, "end": v(8.17, -11.95) * mm});
            skLineSegment(sketch, "E371", {"start": v(8.17, -11.95) * mm, "end": v(8.2, -11.9) * mm});
            skLineSegment(sketch, "E372", {"start": v(8.2, -11.9) * mm, "end": v(8.24, -11.85) * mm});
            skLineSegment(sketch, "E373", {"start": v(8.24, -11.85) * mm, "end": v(8.3, -11.8) * mm});
            skLineSegment(sketch, "E374", {"start": v(8.3, -11.8) * mm, "end": v(8.36, -11.75) * mm});
            skLineSegment(sketch, "E375", {"start": v(8.36, -11.75) * mm, "end": v(8.42, -11.69) * mm});
            skLineSegment(sketch, "E376", {"start": v(8.42, -11.69) * mm, "end": v(8.48, -11.62) * mm});
            skLineSegment(sketch, "E377", {"start": v(8.48, -11.62) * mm, "end": v(8.53, -11.58) * mm});
            skLineSegment(sketch, "E378", {"start": v(8.53, -11.58) * mm, "end": v(8.6, -11.5) * mm});
            skLineSegment(sketch, "E379", {"start": v(8.6, -11.5) * mm, "end": v(8.65, -11.45) * mm});
            skLineSegment(sketch, "E380", {"start": v(8.65, -11.45) * mm, "end": v(8.7, -11.39) * mm});
            skLineSegment(sketch, "E381", {"start": v(8.7, -11.39) * mm, "end": v(8.74, -11.33) * mm});
            skLineSegment(sketch, "E382", {"start": v(8.74, -11.33) * mm, "end": v(8.78, -11.28) * mm});
            skLineSegment(sketch, "E383", {"start": v(8.78, -11.28) * mm, "end": v(8.81, -11.22) * mm});
            skLineSegment(sketch, "E384", {"start": v(8.81, -11.22) * mm, "end": v(8.87, -11.14) * mm});
            skLineSegment(sketch, "E385", {"start": v(8.87, -11.14) * mm, "end": v(8.91, -11.07) * mm});
            skLineSegment(sketch, "E386", {"start": v(8.91, -11.07) * mm, "end": v(8.94, -10.97) * mm});
            skLineSegment(sketch, "E387", {"start": v(8.94, -10.97) * mm, "end": v(8.98, -10.9) * mm});
            skLineSegment(sketch, "E388", {"start": v(8.98, -10.9) * mm, "end": v(9.04, -10.8) * mm});
            skLineSegment(sketch, "E389", {"start": v(9.04, -10.8) * mm, "end": v(9.06, -10.73) * mm});
            skLineSegment(sketch, "E390", {"start": v(9.06, -10.73) * mm, "end": v(9.1, -10.63) * mm});
            skLineSegment(sketch, "E391", {"start": v(9.1, -10.63) * mm, "end": v(9.12, -10.55) * mm});
            skLineSegment(sketch, "E392", {"start": v(9.12, -10.55) * mm, "end": v(9.17, -10.43) * mm});
            skLineSegment(sketch, "E393", {"start": v(9.17, -10.43) * mm, "end": v(9.19, -10.3) * mm});
            skLineSegment(sketch, "E394", {"start": v(9.19, -10.3) * mm, "end": v(9.19, -10.16) * mm});
            skLineSegment(sketch, "E395", {"start": v(9.19, -10.16) * mm, "end": v(9.19, 3.5) * mm});
            skLineSegment(sketch, "E396", {"start": v(9.19, 3.5) * mm, "end": v(-2.7, 0.68) * mm});
            skLineSegment(sketch, "E397", {"start": v(-2.7, 0.68) * mm, "end": v(-2.7, -10.98) * mm});
            skSolve(sketch);
        }
        {
            var Q0;
            Q0=makeQuery(id+"F10.imprint","IMPRINT",FACE,{"disambiguationData":[TD([[makeQuery(id+"F10.imprint","IMPRINT",EDGE,{"derivedFrom":sQuery(id+"F10.wireOp",EDGE,"E113")}),1.0]])]});
            extrude(context, id + "F11", {"entities" : qUnion([Q0]), "operationType" : NewBodyOperationType.ADD, "depth" : 3.17 * mm, "offsetDistance" : 25.4 * mm});
        }
        {
            var Q0;
            Q0=makeQuery(id+"F1.opExtrude","CAP_EDGE",EDGE,{"disambiguationData":[OSD([sQuery(id+"F0.wireOp",EDGE,"E0.left")])],"isStart":false});
            var Q1;
            Q1=makeQuery(id+"F1.opExtrude","CAP_EDGE",EDGE,{"disambiguationData":[OSD([sQuery(id+"F0.wireOp",EDGE,"E0.bottom")])],"isStart":false});
            var Q2;
            Q2=makeQuery(id+"F1.opExtrude","CAP_EDGE",EDGE,{"disambiguationData":[OSD([sQuery(id+"F0.wireOp",EDGE,"E0.right")])],"isStart":false});
            var Q3;
            Q3=makeQuery(id+"F1.opExtrude","CAP_EDGE",EDGE,{"disambiguationData":[OSD([sQuery(id+"F0.wireOp",EDGE,"E0.top")])],"isStart":false});
            fillet(context, id + "F12", {"entities" : qUnion([Q0, Q1, Q2, Q3]), "radius" : 3.17 * mm, "tangentPropagation" : true, "allowEdgeOverflow" : false});
        }
    });
